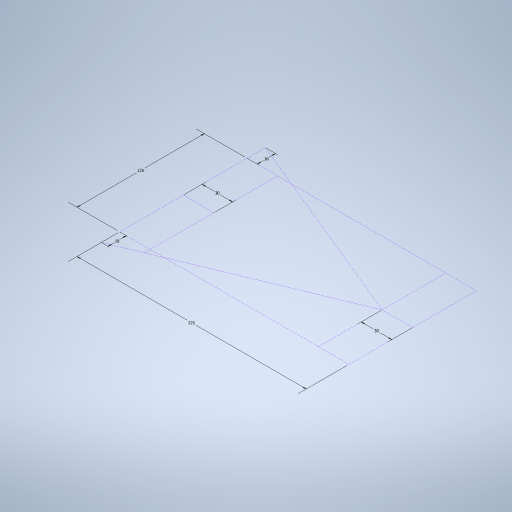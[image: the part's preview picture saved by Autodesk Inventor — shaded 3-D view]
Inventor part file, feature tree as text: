
AUTODESK INVENTOR PART (.ipt)
format: ipt  version: 2024 (Build 280153000, 153)  size: 238,592 bytes
history: native  units: mm
features: sketch x1
ambient origin geometry x8: Origin, YZ Plane, XZ Plane, XY Plane, X Axis, Y Axis, Z Axis, Center Point
feature tree (1):
  sketch  "Sketch1"  dims[d0=225.0mm d1=125.0mm d3=30.0mm d4=30.0mm d5=18.0mm d6=18.0mm]
